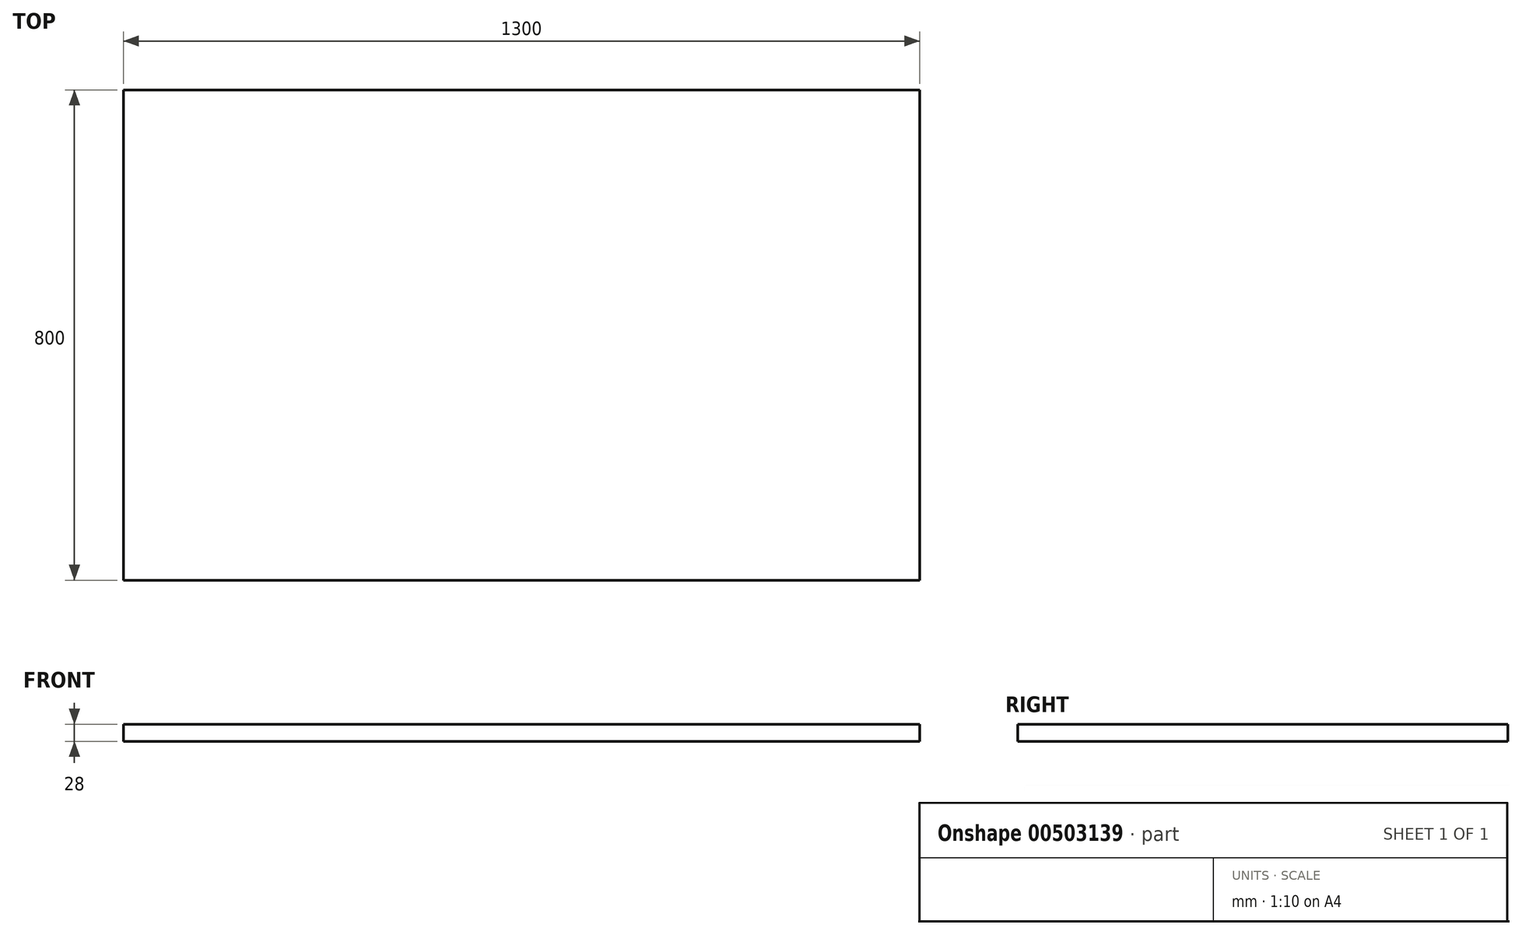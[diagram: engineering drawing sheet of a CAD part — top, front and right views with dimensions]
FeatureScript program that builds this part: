
annotation { "Feature Type Name" : "Feature", "Feature Type Description" : "" }
export const myFeature = defineFeature(function(context is Context, id is Id, definition is map)
    precondition{}
    {
        {
            var Q0;
            Q0=qCreatedBy(makeId("Top.planeOp"),FACE);
            var sketch = newSketch(context, id + "F0", { "sketchPlane" : qUnion([Q0])});
            skLineSegment(sketch, "E0.bottom", {"start": v(-600, -400) * mm, "end": v(700, -400) * mm});
            skLineSegment(sketch, "E0.top", {"start": v(-600, 400) * mm, "end": v(700, 400) * mm});
            skLineSegment(sketch, "E0.left", {"start": v(-600, -400) * mm, "end": v(-600, 400) * mm});
            skLineSegment(sketch, "E0.right", {"start": v(700, -400) * mm, "end": v(700, 400) * mm});
            skSolve(sketch);
        }
        {
            var Q0;
            Q0 = qSketchRegion(id + "F0", true);
            extrude(context, id + "F1", {"entities" : qUnion([Q0]), "depth" : 28 * mm, "offsetDistance" : 25 * mm});
        }
        {
            var Q0;
            Q0=makeQuery(id+"F1.opExtrude","CAP_FACE",FACE,{"disambiguationData":[OSD([sQuery(id+"F0.wireOp",EDGE,"E0.bottom"),sQuery(id+"F0.wireOp",EDGE,"E0.top"),sQuery(id+"F0.wireOp",EDGE,"E0.left"),sQuery(id+"F0.wireOp",EDGE,"E0.right")])],"isStart":true});
            var sketch = newSketch(context, id + "F2", { "sketchPlane" : qUnion([Q0])});
            skLineSegment(sketch, "E1", {"start": v(50, 400) * mm, "end": v(50, -400) * mm, "construction": true});
            skPoint(sketch, "E2", {"position": v(50, 296) * mm});
            skPoint(sketch, "E3", {"position": v(50, -256) * mm});
            skLineSegment(sketch, "E4", {"start": v(-600, 340) * mm, "end": v(700, 340) * mm, "construction": true});
            skSolve(sketch);
        }
    });
